# Revit family: Gira_545200
name_source: partatom
category: Electrical Fixtures
revit_build: Autodesk Revit 2017 (Build: 20160225_1515(x64)
units: mm (PartAtom-declared; Revit-internal decimal feet)

## family parameters
Cut with Voids When Loaded = No
Host = Face
Maintain Annotation Orientation = No
Part Type = Normal
Room Calculation Point = No
Round Connector Dimension = Use Diameter
Shared = No

## types (1)
- WL receiver mod. DRA Gira eNet
    App control via Bluetooth = No
    Applicable with button = No
    Applicable with infrared button = No
    Applicable with movement sensor = No
    Applicable with presence indicator = No
    Applicable with time switch/timer = No
    Applicable with transmission button = No
    BIM = https://media.live.bim.site X1 REG KNX.rfa
    BIMSITE_PRODUCT_ID = 9eb5853e0265f447f9b99469d575ccbd5280435d
    Bus connection included = No
    Cost = 0 $
    Default Elevation = 1219 mm
    Description = WL receiver mod. eNet eNet wireless receiver module,DRA Features: - The eNet wireless reception module is a radio receiver for max. 32 eNet wireless DIN-rail mounting modules. - Operation with power supply. - Integrated antenna. - External antenna can be connected additionally in unfavourable installation conditions.,Notes : - Wireless approval is valid for EU and EFTA countries. - Installation in a distribution box or sub-distribution with a metal housing requires an additional antenna. The additional antenna is to be placed outside the metal housing.
    Dimming phase cut-off = No
    Dimming phase cut-on = No
    GTIN = 4010337774303
    HAN = 545200
    Halogen free = No
    HeinzeBIM = https://www.heinze.de
    Light value memory = No
    Local operation/hand operation = No
    Manufacturer = Gira
    Max. number of venetian-blind outputs = 0
    Max. switching power [Voltampere] = 0
    Modulare Erweiterungsmöglichkeit = No
    Number of binary inputs = 0
    Number of inputs = 0
    Number of outputs = 0
    Parallel-service possible = No
    Power boost suitable = No
    Radio frequent bidirectional = No
    Serial dimmer = No
    Suitable for C-load = No
    Transparent = No
    URL = https://www.gira.de
    Verschiedene Phasen anschließbar = No
    With label area = No
    With switch function = No

## geometry (parser evidence)
native form markers: Blend x2, Sweep x3
no freeform markers — native parametric forms only
